# Revit family: BVN_BPX
name_source: partatom
category: Mechanical Equipment
units: mm (PartAtom-declared; Revit-internal decimal feet)

## family parameters
Always vertical = Yes
Cut with Voids When Loaded = No
OmniClass Number = 23.75.00.00
OmniClass Title = Climate Control (HVAC)
Part Type = Breaks Into
Room Calculation Point = No
Round Connector Dimension = Use Diameter
Shared = No
Work Plane-Based = No

## types (1)
- BVN_BPX
    A = 302 mm  [stored 0.990814 ft]
    Air Flow = 435.0 m³/h
    B = 287 mm  [stored 0.941601 ft]
    C1 = 30 mm  [stored 0.0984252 ft]
    C2 = 30 mm  [stored 0.0984252 ft]
    Capacitor = 2.5
    Current = 0 A
    Description = Duct Fan
    Diameter = 150 mm
    E = 85 mm  [stored 0.278871 ft]
    Frequency = 50 Hz
    Insulation Class = B
    Manufacturer = BVN
    Material = <By Category>
    Model = BPX
    Power = 110 W
    Protection Class = 44
    QD = 149 mm  [stored 0.488845 ft]
    Sound Pressure Level dB(A) = 46
    Speed ( d/d ) = 2600
    Voltage = 230 V
    Weight = 2.70 kg

note: [stored X ft] marks values corroborated as IEEE doubles in the binary element streams (Revit-internal decimal feet)

## geometry (parser evidence)
native form markers: Sweep x3
no freeform markers — native parametric forms only
